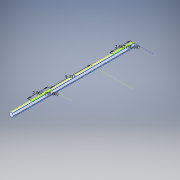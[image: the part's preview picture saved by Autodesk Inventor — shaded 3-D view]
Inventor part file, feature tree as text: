
AUTODESK INVENTOR PART (.ipt)
format: ipt  version: 2017 (Build 210142000, 142)  size: 150,528 bytes
history: native  units: in
note: dims shown in document units (in); Inventor stores cm internally (conversion verified against a paired STEP export)
features: sketch x5, split x1, fillet x1
ambient origin geometry x8: Origin, YZ Plane, XZ Plane, XY Plane, X Axis, Y Axis, Z Axis, Center Point
bodies: Solid1 (feature_tree)
feature tree (7):
  sketch  "Sketch1"  dims[d3=8.5in]
  split  "Split1"
  sketch  "Sketch3"  dims[d7=2.6665in]
  sketch  "Sketch4"  dims[d8=90.0deg]
  sketch  "Sketch5"  dims[d9=2.6665in d10=90.0deg]
  sketch  "Sketch2"  dims[d5=5.333in]
  fillet  "Fillet1"  Radius=16.0in
